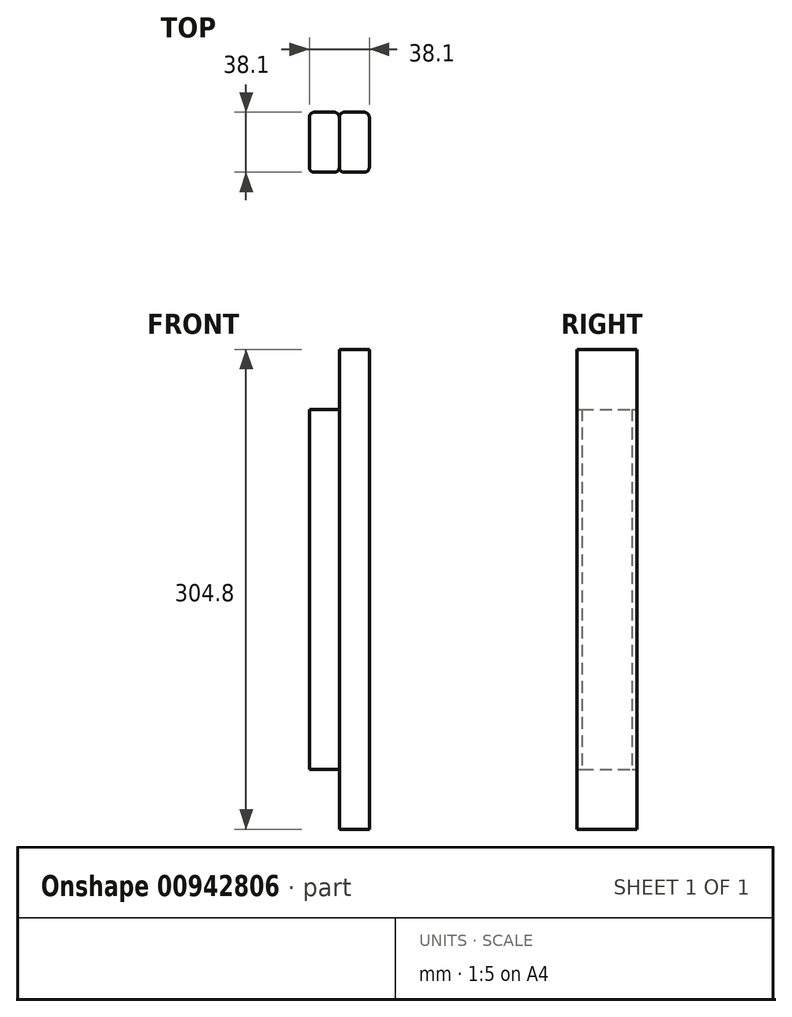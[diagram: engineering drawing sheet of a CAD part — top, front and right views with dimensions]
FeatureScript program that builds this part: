
annotation { "Feature Type Name" : "Feature", "Feature Type Description" : "" }
export const myFeature = defineFeature(function(context is Context, id is Id, definition is map)
    precondition{}
    {
        {
            var Q0;
            Q0=qCreatedBy(makeId("Top.planeOp"),FACE);
            var sketch = newSketch(context, id + "F0", { "sketchPlane" : qUnion([Q0])});
            skLineSegment(sketch, "E0.bottom", {"start": v(3.15, 0) * mm, "end": v(15.9, 0) * mm});
            skLineSegment(sketch, "E0.top", {"start": v(3.15, 38.1) * mm, "end": v(15.9, 38.1) * mm});
            skLineSegment(sketch, "E0.left", {"start": v(0, 3.15) * mm, "end": v(0, 34.95) * mm});
            skLineSegment(sketch, "E0.right", {"start": v(19.05, 3.15) * mm, "end": v(19.05, 34.95) * mm});
            skPoint(sketch, "E1.visualSharp", {"position": v(0, 38.1) * mm});
            skArc(sketch, "E1.filletArc", {"start": v(3.15, 38.1) * mm, "mid": v(0.92, 37.18) * mm, "end": v(0, 34.95) * mm});
            skArc(sketch, "E2.filletArc", {"start": v(19.05, 34.95) * mm, "mid": v(18.13, 37.18) * mm, "end": v(15.9, 38.1) * mm});
            skPoint(sketch, "E3.visualSharp", {"position": v(19.05, 0) * mm});
            skArc(sketch, "E3.filletArc", {"start": v(15.9, 0) * mm, "mid": v(18.13, 0.92) * mm, "end": v(19.05, 3.15) * mm});
            skPoint(sketch, "E4.visualSharp", {"position": v(0, 0) * mm});
            skArc(sketch, "E4.filletArc", {"start": v(0, 3.15) * mm, "mid": v(0.92, 0.92) * mm, "end": v(3.15, 0) * mm});
            skLineSegment(sketch, "E5.bottom", {"start": v(22.2, 0) * mm, "end": v(34.95, 0) * mm});
            skLineSegment(sketch, "E5.right", {"start": v(38.1, 3.15) * mm, "end": v(38.1, 34.95) * mm});
            skArc(sketch, "E6.filletArc", {"start": v(22.2, 38.1) * mm, "mid": v(19.97, 37.18) * mm, "end": v(19.05, 34.95) * mm});
            skArc(sketch, "E7.filletArc", {"start": v(38.1, 34.95) * mm, "mid": v(37.18, 37.18) * mm, "end": v(34.95, 38.1) * mm});
            skArc(sketch, "E8.filletArc", {"start": v(34.95, 0) * mm, "mid": v(37.18, 0.92) * mm, "end": v(38.1, 3.15) * mm});
            skArc(sketch, "E9.filletArc", {"start": v(19.05, 3.15) * mm, "mid": v(19.97, 0.92) * mm, "end": v(22.2, 0) * mm});
            skLineSegment(sketch, "E10", {"start": v(22.2, 38.1) * mm, "end": v(34.95, 38.1) * mm});
            skSolve(sketch);
        }
        {
            var Q0;
            Q0=makeQuery(id+"F0.imprint","IMPRINT",FACE,{"disambiguationData":[TD([[makeQuery(id+"F0.imprint","IMPRINT",EDGE,{"derivedFrom":sQuery(id+"F0.wireOp",EDGE,"E5.bottom")}),1.0]])]});
            var Q1;
            Q1=makeQuery(id+"F0.imprint","IMPRINT",FACE,{"disambiguationData":[TD([[makeQuery(id+"F0.imprint","IMPRINT",EDGE,{"derivedFrom":sQuery(id+"F0.wireOp",EDGE,"b7ff1907-7b2b-4cdd-8ea5-b45dade5522d.bottom")}),1.0]])]});
            var Q2;
            Q2=makeQuery(id+"F0.imprint","IMPRINT",FACE,{"disambiguationData":[TD([[makeQuery(id+"F0.imprint","IMPRINT",EDGE,{"derivedFrom":sQuery(id+"F0.wireOp",EDGE,"66c86851-db75-4c71-9093-7621e61d7ab7.bottom")}),1.0]])]});
            extrude(context, id + "F1", {"entities" : qUnion([Q0, Q1, Q2]), "depth" : 304.8 * mm, "offsetDistance" : 25.4 * mm});
        }
        {
            var Q0;
            Q0=qSketchRegion(id+"F0",true);
            extrude(context, id + "F2", {"entities" : qUnion([Q0]), "operationType" : NewBodyOperationType.ADD, "depth" : 266.7 * mm, "offsetDistance" : 25.4 * mm});
        }
        {
            var Q0;
            Q0=makeQuery(id+"F0.imprint","IMPRINT",FACE,{"disambiguationData":[TD([[makeQuery(id+"F0.imprint","IMPRINT",EDGE,{"derivedFrom":sQuery(id+"F0.wireOp",EDGE,"E0.bottom")}),1.0]])]});
            extrude(context, id + "F3", {"entities" : qUnion([Q0]), "operationType" : NewBodyOperationType.REMOVE, "depth" : 38.1 * mm, "offsetDistance" : 25.4 * mm});
        }
    });
